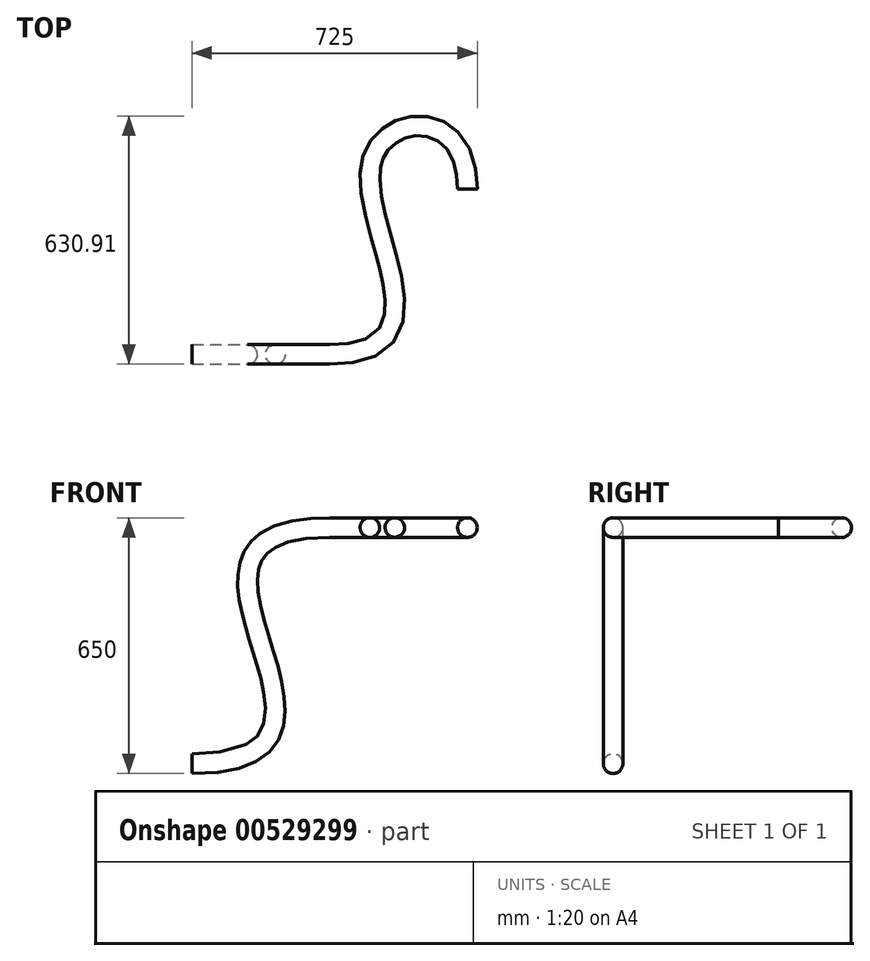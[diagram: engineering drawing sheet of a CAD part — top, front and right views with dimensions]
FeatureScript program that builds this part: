
annotation { "Feature Type Name" : "Feature", "Feature Type Description" : "" }
export const myFeature = defineFeature(function(context is Context, id is Id, definition is map)
    precondition{}
    {
        {
            var Q0;
            Q0=qCreatedBy(makeId("Front.planeOp"),FACE);
            var sketch = newSketch(context, id + "F0", { "sketchPlane" : qUnion([Q0])});
            skFitSpline(sketch, "E0", {"points": [v(0, 0) * mm, v(350, 600) * mm], "startDerivative": vector(1610.84, 0) * mm, "endDerivative": vector(1596.17, 0) * mm});
            skSolve(sketch);
        }
        {
            var Q0;
            Q0=qCreatedBy(makeId("Top.planeOp"),FACE);
            var Q1;
            Q1=sQuery(id+"F0.wireOp",VERTEX,"E0.end");
            cPlane(context, id + "F1", {"entities" : qUnion([Q0, Q1]), "cplaneType" : CPlaneType.PLANE_POINT, "offset" : 25 * mm, "width" : 150 * mm, "height" : 150 * mm});
        }
        {
            var Q0;
            Q0=qCreatedBy(id+"F1.planeOp",FACE);
            var sketch = newSketch(context, id + "F2", { "sketchPlane" : qUnion([Q0])});
            skPoint(sketch, "E1.0", {"position": v(350, 0) * mm});
            skFitSpline(sketch, "E2", {"points": [v(350, 0) * mm, v(459.71, 500) * mm, v(700, 420) * mm], "startDerivative": vector(1687.99, 0) * mm, "endDerivative": vector(0, -1518.14) * mm});
            skSolve(sketch);
        }
        {
            var Q0;
            Q0=qCreatedBy(makeId("Right.planeOp"),FACE);
            var sketch = newSketch(context, id + "F3", { "sketchPlane" : qUnion([Q0])});
            skCircle(sketch, "E3", {"center": v(0, 0) * mm, "radius": 25 * mm});
            skSolve(sketch);
        }
        {
            var Q0;
            Q0=makeQuery(id+"F3.imprint","IMPRINT",FACE,{"disambiguationData":[TD([[makeQuery(id+"F3.imprint","IMPRINT",EDGE,{"derivedFrom":sQuery(id+"F3.wireOp",EDGE,"E3")}),1.0]])]});
            var Q1;
            Q1=sQuery(id+"F0.wireOp",EDGE,"E0");
            var Q2;
            Q2=sQuery(id+"F2.wireOp",EDGE,"E2");
            sweep(context, id + "F4", {"profiles" : qUnion([Q0]), "path" : qUnion([Q1, Q2])});
        }
    });
